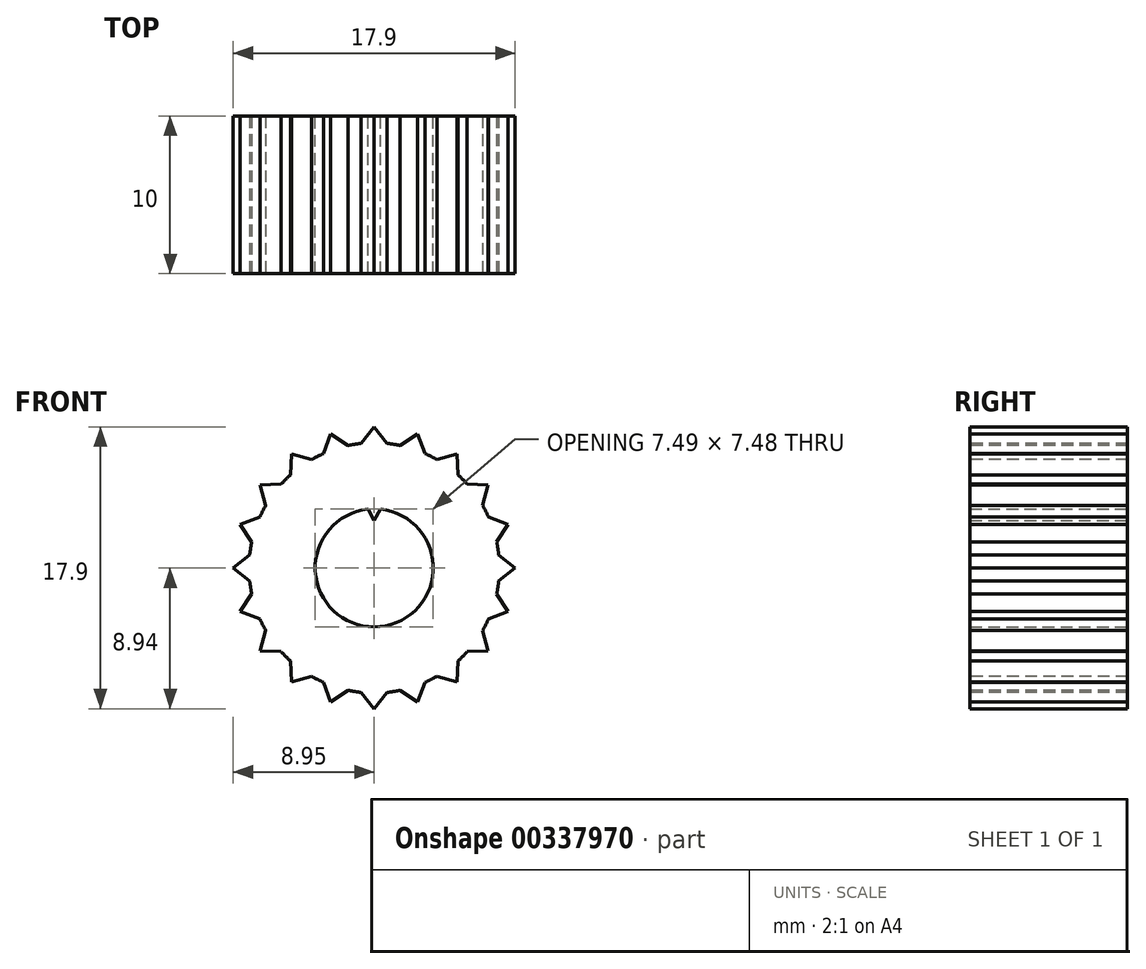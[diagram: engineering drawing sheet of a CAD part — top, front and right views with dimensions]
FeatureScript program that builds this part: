
annotation { "Feature Type Name" : "Feature", "Feature Type Description" : "" }
export const myFeature = defineFeature(function(context is Context, id is Id, definition is map)
    precondition{}
    {
        {
            var Q0;
            Q0=qCreatedBy(makeId("Front.planeOp"),FACE);
            var sketch = newSketch(context, id + "F0", { "sketchPlane" : qUnion([Q0])});
            skCircle(sketch, "E0", {"center": v(0, 0) * mm, "radius": 3 * mm});
            skCircle(sketch, "E1", {"center": v(0, 0) * mm, "radius": 7.95 * mm});
            skCircle(sketch, "E2", {"center": v(0, 0) * mm, "radius": 3.75 * mm});
            skCircle(sketch, "E3", {"center": v(0, 0) * mm, "radius": 8.95 * mm, "construction": true});
            skLineSegment(sketch, "E4", {"start": v(0, 8.95) * mm, "end": v(0, 0) * mm, "construction": true});
            skSolve(sketch);
        }
        {
            var Q0;
            Q0=makeQuery(id+"F0.imprint","IMPRINT",FACE,{"disambiguationData":[TD([[makeQuery(id+"F0.imprint","IMPRINT",EDGE,{"derivedFrom":sQuery(id+"F0.wireOp",EDGE,"E2")}),-1.0]])]});
            extrude(context, id + "F1", {"entities" : qUnion([Q0]), "depth" : 10 * mm});
        }
        {
            var Q0;
            Q0=makeQuery(id+"F1.opExtrude","CAP_FACE",FACE,{"disambiguationData":[OSD([sQuery(id+"F0.wireOp",EDGE,"E1"),sQuery(id+"F0.wireOp",EDGE,"E2")])],"isStart":false});
            var sketch = newSketch(context, id + "F2", { "sketchPlane" : qUnion([Q0])});
            skLineSegment(sketch, "E5", {"start": v(0, 7.95) * mm, "end": v(0, 0) * mm, "construction": true});
            skCircle(sketch, "E6.0", {"center": v(0, 0) * mm, "radius": 7.95 * mm});
            skLineSegment(sketch, "E7", {"start": v(-0.83, 7.9) * mm, "end": v(0, 8.95) * mm});
            skLineSegment(sketch, "E8", {"start": v(0, 8.95) * mm, "end": v(0.83, 7.9) * mm});
            skLineSegment(sketch, "E9", {"start": v(0.83, 7.9) * mm, "end": v(-0.83, 7.9) * mm});
            skLineSegment(sketch, "E10", {"start": v(0, 0) * mm, "end": v(-0.83, 7.9) * mm, "construction": true});
            skLineSegment(sketch, "E11", {"start": v(0, 0) * mm, "end": v(0.83, 7.9) * mm, "construction": true});
            skCircle(sketch, "E12", {"center": v(0, 0) * mm, "radius": 8.95 * mm, "construction": true});
            skSolve(sketch);
        }
        {
            var Q0;
            {var subQ1=sQuery(id+"F2.wireOp",EDGE,"E7");Q0=makeQuery(id+"F2.imprint","IMPRINT",FACE,{"disambiguationData":[TD([[makeQuery(id+"F2.imprint","IMPRINT",EDGE,{"derivedFrom":subQ1}),-1.0]])]});}
            var Q1;
            Q1=makeQuery(id+"F1.opExtrude","CAP_FACE",FACE,{"disambiguationData":[OSD([sQuery(id+"F0.wireOp",EDGE,"E1"),sQuery(id+"F0.wireOp",EDGE,"E2")])],"isStart":true});
            extrude(context, id + "F3", {"entities" : qUnion([Q0]), "operationType" : NewBodyOperationType.ADD, "endBound" : BoundingType.UP_TO_SURFACE, "oppositeDirection" : true, "endBoundEntityFace" : qUnion([Q1]), "depth" : 25.4 * mm});
        }
        {
            var Q0;
            Q0=makeQuery(id+"F1.opExtrude","SWEPT_BODY",BODY,{"disambiguationData":[OSD([sQuery(id+"F0.wireOp",EDGE,"E1"),sQuery(id+"F0.wireOp",EDGE,"E2")])]});
            var Q1;
            Q1=makeQuery(id+"F1.opExtrude","SWEPT_FACE",FACE,{"disambiguationData":[OSD([sQuery(id+"F0.wireOp",EDGE,"E2")])]});
            circularPattern(context, id + "F4", {"operationType" : NewBodyOperationType.ADD, "entities" : qUnion([Q0]), "axis" : qUnion([Q1]), "angle" : 360 * degree, "instanceCount" : 20, "equalSpace" : true});
        }
        {
            var Q0;
            {var subQ0=sQuery(id+"F0.wireOp",EDGE,"E2");var subQ1=sQuery(id+"F0.wireOp",EDGE,"E1");var subQ2=makeQuery(id+"F3.boolean.opBoolean","MERGE",FACE,{"derivedFrom":[makeQuery(id+"F1.opExtrude","CAP_FACE",FACE,{"disambiguationData":[OSD([subQ1,subQ0])],"isStart":true}),makeQuery(id+"F3.opExtrude","CAP_FACE",FACE,{"disambiguationData":[OSD([subQ1,subQ0])],"isStart":false})]});Q0=makeQuery(id+"F4.boolean.opBoolean","MERGE",FACE,{"derivedFrom":[subQ2,makeQuery(id+"F4.opPattern","COPY",FACE,{"derivedFrom":subQ2,"instanceName":"1"}),makeQuery(id+"F4.opPattern","COPY",FACE,{"derivedFrom":subQ2,"instanceName":"2"}),makeQuery(id+"F4.opPattern","COPY",FACE,{"derivedFrom":subQ2,"instanceName":"3"}),makeQuery(id+"F4.opPattern","COPY",FACE,{"derivedFrom":subQ2,"instanceName":"4"}),makeQuery(id+"F4.opPattern","COPY",FACE,{"derivedFrom":subQ2,"instanceName":"5"}),makeQuery(id+"F4.opPattern","COPY",FACE,{"derivedFrom":subQ2,"instanceName":"6"}),makeQuery(id+"F4.opPattern","COPY",FACE,{"derivedFrom":subQ2,"instanceName":"7"}),makeQuery(id+"F4.opPattern","COPY",FACE,{"derivedFrom":subQ2,"instanceName":"8"}),makeQuery(id+"F4.opPattern","COPY",FACE,{"derivedFrom":subQ2,"instanceName":"9"}),makeQuery(id+"F4.opPattern","COPY",FACE,{"derivedFrom":subQ2,"instanceName":"10"}),makeQuery(id+"F4.opPattern","COPY",FACE,{"derivedFrom":subQ2,"instanceName":"11"}),makeQuery(id+"F4.opPattern","COPY",FACE,{"derivedFrom":subQ2,"instanceName":"12"}),makeQuery(id+"F4.opPattern","COPY",FACE,{"derivedFrom":subQ2,"instanceName":"13"}),makeQuery(id+"F4.opPattern","COPY",FACE,{"derivedFrom":subQ2,"instanceName":"14"}),makeQuery(id+"F4.opPattern","COPY",FACE,{"derivedFrom":subQ2,"instanceName":"15"}),makeQuery(id+"F4.opPattern","COPY",FACE,{"derivedFrom":subQ2,"instanceName":"16"}),makeQuery(id+"F4.opPattern","COPY",FACE,{"derivedFrom":subQ2,"instanceName":"17"}),makeQuery(id+"F4.opPattern","COPY",FACE,{"derivedFrom":subQ2,"instanceName":"18"}),makeQuery(id+"F4.opPattern","COPY",FACE,{"derivedFrom":subQ2,"instanceName":"19"}),makeQuery(id+"F4.opPattern","COPY",FACE,{"derivedFrom":subQ2,"instanceName":"20"}),makeQuery(id+"F4.opPattern","COPY",FACE,{"derivedFrom":subQ2,"instanceName":"21"}),makeQuery(id+"F4.opPattern","COPY",FACE,{"derivedFrom":subQ2,"instanceName":"22"}),makeQuery(id+"F4.opPattern","COPY",FACE,{"derivedFrom":subQ2,"instanceName":"23"}),makeQuery(id+"F4.opPattern","COPY",FACE,{"derivedFrom":subQ2,"instanceName":"24"}),makeQuery(id+"F4.opPattern","COPY",FACE,{"derivedFrom":subQ2,"instanceName":"25"}),makeQuery(id+"F4.opPattern","COPY",FACE,{"derivedFrom":subQ2,"instanceName":"26"}),makeQuery(id+"F4.opPattern","COPY",FACE,{"derivedFrom":subQ2,"instanceName":"27"}),makeQuery(id+"F4.opPattern","COPY",FACE,{"derivedFrom":subQ2,"instanceName":"28"}),makeQuery(id+"F4.opPattern","COPY",FACE,{"derivedFrom":subQ2,"instanceName":"29"})]});}
            var sketch = newSketch(context, id + "F5", { "sketchPlane" : qUnion([Q0])});
            skPoint(sketch, "E13.0", {"position": v(0, 0) * mm});
            skCircle(sketch, "E14", {"center": v(0, 0) * mm, "radius": 3 * mm, "construction": true});
            skLineSegment(sketch, "E15", {"start": v(0, 0) * mm, "end": v(0, 3.75) * mm, "construction": true});
            skLineSegment(sketch, "E16", {"start": v(0, 3) * mm, "end": v(-0.4, 3.73) * mm});
            skLineSegment(sketch, "E17", {"start": v(-0.4, 3.73) * mm, "end": v(0, 4.06) * mm});
            skLineSegment(sketch, "E18", {"start": v(0, 4.06) * mm, "end": v(0.4, 3.73) * mm});
            skLineSegment(sketch, "E19", {"start": v(0.4, 3.73) * mm, "end": v(0, 3) * mm});
            skLineSegment(sketch, "E20", {"start": v(0, 0) * mm, "end": v(-0.4, 3.73) * mm, "construction": true});
            skSolve(sketch);
        }
        {
            var Q0;
            {var subQ0=sQuery(id+"F5.wireOp",EDGE,"E16");Q0=makeQuery(id+"F5.imprint","IMPRINT",FACE,{"disambiguationData":[TD([[makeQuery(id+"F5.imprint","IMPRINT",EDGE,{"derivedFrom":subQ0}),-1.0]])]});}
            var Q1;
            {var subQ0=sQuery(id+"F5.wireOp",EDGE,"E17");Q1=makeQuery(id+"F5.imprint","IMPRINT",FACE,{"disambiguationData":[TD([[makeQuery(id+"F5.imprint","IMPRINT",EDGE,{"derivedFrom":subQ0}),-1.0]])]});}
            var Q2;
            {var subQ0=makeQuery(id+"F3.boolean.opBoolean","MERGE",FACE,{"derivedFrom":[makeQuery(id+"F1.opExtrude","CAP_FACE",FACE,{"disambiguationData":[OSD([sQuery(id+"F0.wireOp",EDGE,"E1"),sQuery(id+"F0.wireOp",EDGE,"E2")])],"isStart":false}),makeQuery(id+"F3.opExtrude","CAP_FACE",FACE,{"disambiguationData":[OSD([sQuery(id+"F2.wireOp",EDGE,"E6.0"),sQuery(id+"F2.wireOp",EDGE,"E7"),sQuery(id+"F2.wireOp",EDGE,"E8")])],"isStart":true})]});Q2=makeQuery(id+"F4.boolean.opBoolean","MERGE",FACE,{"derivedFrom":[subQ0,makeQuery(id+"F4.opPattern","COPY",FACE,{"derivedFrom":subQ0,"instanceName":"1"}),makeQuery(id+"F4.opPattern","COPY",FACE,{"derivedFrom":subQ0,"instanceName":"2"}),makeQuery(id+"F4.opPattern","COPY",FACE,{"derivedFrom":subQ0,"instanceName":"3"}),makeQuery(id+"F4.opPattern","COPY",FACE,{"derivedFrom":subQ0,"instanceName":"4"}),makeQuery(id+"F4.opPattern","COPY",FACE,{"derivedFrom":subQ0,"instanceName":"5"}),makeQuery(id+"F4.opPattern","COPY",FACE,{"derivedFrom":subQ0,"instanceName":"6"}),makeQuery(id+"F4.opPattern","COPY",FACE,{"derivedFrom":subQ0,"instanceName":"7"}),makeQuery(id+"F4.opPattern","COPY",FACE,{"derivedFrom":subQ0,"instanceName":"8"}),makeQuery(id+"F4.opPattern","COPY",FACE,{"derivedFrom":subQ0,"instanceName":"9"}),makeQuery(id+"F4.opPattern","COPY",FACE,{"derivedFrom":subQ0,"instanceName":"10"}),makeQuery(id+"F4.opPattern","COPY",FACE,{"derivedFrom":subQ0,"instanceName":"11"}),makeQuery(id+"F4.opPattern","COPY",FACE,{"derivedFrom":subQ0,"instanceName":"12"}),makeQuery(id+"F4.opPattern","COPY",FACE,{"derivedFrom":subQ0,"instanceName":"13"}),makeQuery(id+"F4.opPattern","COPY",FACE,{"derivedFrom":subQ0,"instanceName":"14"}),makeQuery(id+"F4.opPattern","COPY",FACE,{"derivedFrom":subQ0,"instanceName":"15"}),makeQuery(id+"F4.opPattern","COPY",FACE,{"derivedFrom":subQ0,"instanceName":"16"}),makeQuery(id+"F4.opPattern","COPY",FACE,{"derivedFrom":subQ0,"instanceName":"17"}),makeQuery(id+"F4.opPattern","COPY",FACE,{"derivedFrom":subQ0,"instanceName":"18"}),makeQuery(id+"F4.opPattern","COPY",FACE,{"derivedFrom":subQ0,"instanceName":"19"}),makeQuery(id+"F4.opPattern","COPY",FACE,{"derivedFrom":subQ0,"instanceName":"20"}),makeQuery(id+"F4.opPattern","COPY",FACE,{"derivedFrom":subQ0,"instanceName":"21"}),makeQuery(id+"F4.opPattern","COPY",FACE,{"derivedFrom":subQ0,"instanceName":"22"}),makeQuery(id+"F4.opPattern","COPY",FACE,{"derivedFrom":subQ0,"instanceName":"23"}),makeQuery(id+"F4.opPattern","COPY",FACE,{"derivedFrom":subQ0,"instanceName":"24"}),makeQuery(id+"F4.opPattern","COPY",FACE,{"derivedFrom":subQ0,"instanceName":"25"}),makeQuery(id+"F4.opPattern","COPY",FACE,{"derivedFrom":subQ0,"instanceName":"26"}),makeQuery(id+"F4.opPattern","COPY",FACE,{"derivedFrom":subQ0,"instanceName":"27"}),makeQuery(id+"F4.opPattern","COPY",FACE,{"derivedFrom":subQ0,"instanceName":"28"}),makeQuery(id+"F4.opPattern","COPY",FACE,{"derivedFrom":subQ0,"instanceName":"29"})]});}
            extrude(context, id + "F6", {"entities" : qUnion([Q0, Q1]), "operationType" : NewBodyOperationType.ADD, "endBound" : BoundingType.UP_TO_SURFACE, "oppositeDirection" : true, "endBoundEntityFace" : qUnion([Q2]), "depth" : 25.4 * mm});
        }
    });
